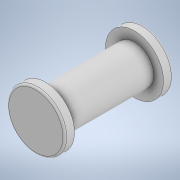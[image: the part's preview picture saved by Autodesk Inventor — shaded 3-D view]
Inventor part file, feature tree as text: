
AUTODESK INVENTOR PART (.ipt)
format: ipt  version: 2021 (Build 250183000, 183)  size: 125,440 bytes
history: native  units: in
note: dims shown in document units (in); Inventor stores cm internally (conversion verified against a paired STEP export)
features: extrude x3, sketch x3, plane x2, fillet x1
ambient origin geometry x8: Origin, YZ Plane, XZ Plane, XY Plane, X Axis, Y Axis, Z Axis, Center Point
bodies: Solid1 (feature_tree)
feature tree (9):
  extrude  "Extrusion1"  Depth=0.1811in TaperAngle=0.0deg
  plane  "Work Plane1"
  plane  "Work Plane2"
  extrude  "Extrusion2"  TaperAngle=0.0deg  [1 undecoded]
  extrude  "Extrusion3"  Depth=0.0197in TaperAngle=0.0deg
  fillet  "Fillet1"  Radius=0.1181in
  sketch  "Sketch1"  dims[d0=0.0787in d1=0.1811in d2=0.0in]
  sketch  "Sketch2"  dims[d3=0.0in d4=0.0in]
  sketch  "Sketch3"  dims[d5=0.1181in d6=0.0197in d7=0.0in d8=0.1181in d9=0.0197in d10=0.0in d11=0.0039in]
note: 1 required parameter value undecoded (feature->parameter linkage not recoverable at this tier; creation-order binding heuristic only, values carry confidence <= 0.55)
